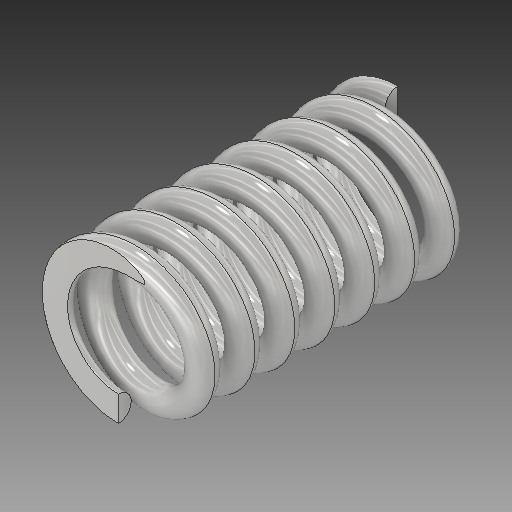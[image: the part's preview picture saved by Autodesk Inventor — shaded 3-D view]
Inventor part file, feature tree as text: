
AUTODESK INVENTOR PART (.ipt)
format: ipt  version: 2018 (Build 220112000, 112)  size: 595,968 bytes
history: native  units: in
note: dims shown in document units (in); Inventor stores cm internally (conversion verified against a paired STEP export)
features: sketch x3, extrude x2, helix x1, plane x1
ambient origin geometry x8: Origin, YZ Plane, XZ Plane, XY Plane, X Axis, Y Axis, Z Axis, Center Point
bodies: Solid1 (feature_tree)
feature tree (7):
  helix  "Coil1"  [1 undecoded]
  extrude  "Extrusion1"  Depth=0.4331in TaperAngle=0.0deg
  plane  "Work Plane1"
  extrude  "Extrusion2"  Depth=0.4331in TaperAngle=0.0deg
  sketch  "Sketch1"  dims[d3=0.2362in]
  sketch  "Sketch2"  dims[d4=0.3937in d5=0.4331in d6=2.6575in d7=0.0in d8=90.0deg d9=45.0deg d10=90.0deg d11=45.0deg d12=0.3937in d13=0.0in]
  sketch  "Sketch4"  dims[d14=0.4331in d15=0.3937in d16=0.0in]
note: 1 required parameter value undecoded (feature->parameter linkage not recoverable at this tier; creation-order binding heuristic only, values carry confidence <= 0.55)
